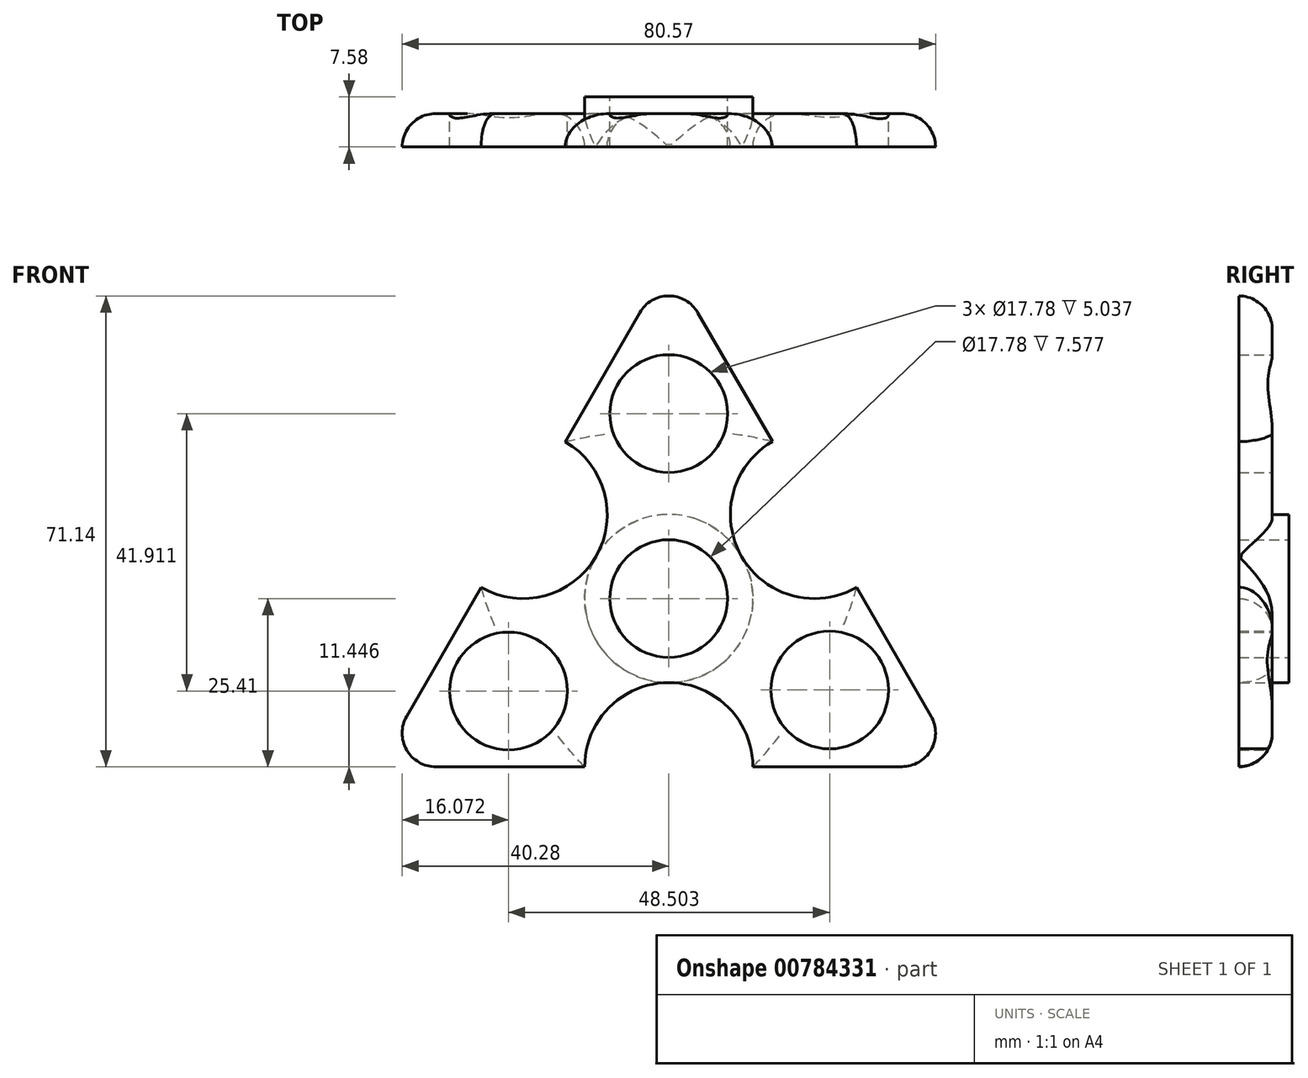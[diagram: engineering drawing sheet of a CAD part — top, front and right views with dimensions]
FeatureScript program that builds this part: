
annotation { "Feature Type Name" : "Feature", "Feature Type Description" : "" }
export const myFeature = defineFeature(function(context is Context, id is Id, definition is map)
    precondition{}
    {
        {
            var Q0;
            Q0=qCreatedBy(makeId("Front.planeOp"),FACE);
            var sketch = newSketch(context, id + "F0", { "sketchPlane" : qUnion([Q0])});
            skCircle(sketch, "E0.cCircle", {"center": v(0, 0) * mm, "radius": 25.4 * mm, "construction": true});
            skLineSegment(sketch, "E0.0", {"start": v(-0.01, 50.8) * mm, "end": v(44, -25.4) * mm});
            skLineSegment(sketch, "E0.1", {"start": v(44, -25.4) * mm, "end": v(-44, -25.41) * mm});
            skLineSegment(sketch, "E0.2", {"start": v(-44, -25.41) * mm, "end": v(-0.01, 50.8) * mm});
            skPoint(sketch, "E0.0.midPoint", {"position": v(22, 12.7) * mm});
            skCircle(sketch, "E1", {"center": v(-22, 12.7) * mm, "radius": 12.7 * mm});
            skCircle(sketch, "E2", {"center": v(0, -25.4) * mm, "radius": 12.7 * mm});
            skPoint(sketch, "E2.centerSnap0", {"position": v(0, -25.4) * mm});
            skCircle(sketch, "E3", {"center": v(22, 12.7) * mm, "radius": 12.7 * mm});
            skSolve(sketch);
        }
        {
            var Q0;
            {var subQ1=sQuery(id+"F0.wireOp",EDGE,"E0.0");var subQ8=sQuery(id+"F0.wireOp",EDGE,"E0.2");var subQ11=makeQuery(id+"F0.imprint","INTERSECT",VERTEX,{"derivedFrom":[subQ1,subQ8]});Q0=makeQuery(id+"F0.imprint","IMPRINT",FACE,{"disambiguationData":[TD([[makeQuery(id+"F0.imprint","IMPRINT",EDGE,{"disambiguationData":[TD([[subQ11,-1.0]])],"derivedFrom":subQ1}),-1.0]])]});}
            extrude(context, id + "F1", {"entities" : qUnion([Q0]), "depth" : 7.62 * mm, "offsetDistance" : 25.4 * mm});
        }
        {
            var Q0;
            Q0=makeQuery(id+"F1.opExtrude","CAP_FACE",FACE,{"disambiguationData":[OSD([sQuery(id+"F0.wireOp",EDGE,"E0.0"),sQuery(id+"F0.wireOp",EDGE,"E0.1"),sQuery(id+"F0.wireOp",EDGE,"E0.2"),sQuery(id+"F0.wireOp",EDGE,"E1"),sQuery(id+"F0.wireOp",EDGE,"E2"),sQuery(id+"F0.wireOp",EDGE,"E3")])],"isStart":false});
            var sketch = newSketch(context, id + "F2", { "sketchPlane" : qUnion([Q0])});
            skCircle(sketch, "E4", {"center": v(0, 0) * mm, "radius": 12.7 * mm});
            skSolve(sketch);
        }
        {
            var Q0;
            Q0=qSketchRegion(id+"F2",true);
            extrude(context, id + "F3", {"entities" : qUnion([Q0]), "operationType" : NewBodyOperationType.ADD, "depth" : 2.54 * mm, "offsetDistance" : 25.4 * mm, "hasSecondDirection" : true, "secondDirectionOppositeDirection" : true, "secondDirectionDepth" : 10.16 * mm});
        }
        {
            var Q0;
            Q0=makeQuery(id+"F3.opExtrude","CAP_FACE",FACE,{"disambiguationData":[OSD([sQuery(id+"F2.wireOp",EDGE,"E4")])],"isStart":true});
            var sketch = newSketch(context, id + "F4", { "sketchPlane" : qUnion([Q0])});
            skCircle(sketch, "E5", {"center": v(0, 0) * mm, "radius": 8.9 * mm});
            skSolve(sketch);
        }
        {
            var Q0;
            Q0=qSketchRegion(id+"F4",true);
            extrude(context, id + "F5", {"entities" : qUnion([Q0]), "operationType" : NewBodyOperationType.REMOVE, "oppositeDirection" : true, "depth" : 25.4 * mm, "offsetDistance" : 25.4 * mm});
        }
        {
            var Q0;
            Q0=qCreatedBy(makeId("Top.planeOp"),FACE);
            var sketch = newSketch(context, id + "F6", { "sketchPlane" : qUnion([Q0])});
            skLineSegment(sketch, "E6.bottom", {"start": v(-45.33, -5.04) * mm, "end": v(58.86, -5.04) * mm});
            skLineSegment(sketch, "E6.top", {"start": v(-45.33, -12.1) * mm, "end": v(58.86, -12.1) * mm});
            skLineSegment(sketch, "E6.left", {"start": v(-45.33, -5.04) * mm, "end": v(-45.33, -12.1) * mm});
            skLineSegment(sketch, "E6.right", {"start": v(58.86, -5.04) * mm, "end": v(58.86, -12.1) * mm});
            skSolve(sketch);
        }
        {
            var Q0;
            Q0=qSketchRegion(id+"F6",true);
            extrude(context, id + "F7", {"entities" : qUnion([Q0]), "operationType" : NewBodyOperationType.REMOVE, "depth" : 66.04 * mm, "offsetDistance" : 25.4 * mm, "hasSecondDirection" : true, "secondDirectionOppositeDirection" : true, "secondDirectionDepth" : 38.86 * mm});
        }
        {
            var Q0;
            Q0=makeQuery(id+"F1.opExtrude","CAP_FACE",FACE,{"disambiguationData":[OSD([sQuery(id+"F0.wireOp",EDGE,"E0.0"),sQuery(id+"F0.wireOp",EDGE,"E0.1"),sQuery(id+"F0.wireOp",EDGE,"E0.2"),sQuery(id+"F0.wireOp",EDGE,"E1"),sQuery(id+"F0.wireOp",EDGE,"E2"),sQuery(id+"F0.wireOp",EDGE,"E3")])],"isStart":true});
            var sketch = newSketch(context, id + "F8", { "sketchPlane" : qUnion([Q0])});
            skCircle(sketch, "E7", {"center": v(0, 27.95) * mm, "radius": 8.9 * mm});
            skCircle(sketch, "E8", {"center": v(-24.3, -13.82) * mm, "radius": 8.9 * mm});
            skCircle(sketch, "E9", {"center": v(24.2, -13.96) * mm, "radius": 8.9 * mm});
            skSolve(sketch);
        }
        {
            var Q0;
            Q0=qSketchRegion(id+"F8",true);
            extrude(context, id + "F9", {"entities" : qUnion([Q0]), "operationType" : NewBodyOperationType.REMOVE, "oppositeDirection" : true, "depth" : 25.4 * mm, "offsetDistance" : 25.4 * mm});
        }
        {
            var Q0;
            Q0=makeQuery(id+"F1.opExtrude","SWEPT_EDGE",EDGE,{"disambiguationData":[OSD([sQuery(id+"F0.wireOp",EDGE,"E0.0"),sQuery(id+"F0.wireOp",EDGE,"E0.2")])]});
            var Q1;
            Q1=makeQuery(id+"F1.opExtrude","SWEPT_EDGE",EDGE,{"disambiguationData":[OSD([sQuery(id+"F0.wireOp",EDGE,"E0.0"),sQuery(id+"F0.wireOp",EDGE,"E0.1")])]});
            var Q2;
            Q2=makeQuery(id+"F1.opExtrude","SWEPT_EDGE",EDGE,{"disambiguationData":[OSD([sQuery(id+"F0.wireOp",EDGE,"E0.1"),sQuery(id+"F0.wireOp",EDGE,"E0.2")])]});
            fillet(context, id + "F10", {"entities" : qUnion([Q0, Q1, Q2]), "radius" : 5.08 * mm, "tangentPropagation" : true, "allowEdgeOverflow" : false});
        }
        {
            var Q0;
            {var subQ0=sQuery(id+"F0.wireOp",EDGE,"E0.1");Q0=makeQuery(id+"F1.opExtrude","CAP_EDGE",EDGE,{"disambiguationData":[OSD([subQ0]),TDD([makeQuery(id+"F0.imprint","IMPRINT",EDGE,{"disambiguationData":[TD([[makeQuery(id+"F0.imprint","INTERSECT",VERTEX,{"derivedFrom":[subQ0,sQuery(id+"F0.wireOp",EDGE,"E0.2")]}),1.0]])],"derivedFrom":subQ0})])],"isStart":true});}
            var Q1;
            {var subQ0=sQuery(id+"F0.wireOp",EDGE,"E0.1");Q1=makeQuery(id+"F1.opExtrude","CAP_EDGE",EDGE,{"disambiguationData":[OSD([subQ0]),TDD([makeQuery(id+"F0.imprint","IMPRINT",EDGE,{"disambiguationData":[TD([[makeQuery(id+"F0.imprint","INTERSECT",VERTEX,{"derivedFrom":[sQuery(id+"F0.wireOp",EDGE,"E0.0"),subQ0]}),-1.0]])],"derivedFrom":subQ0})])],"isStart":true});}
            var Q2;
            {var subQ0=sQuery(id+"F0.wireOp",EDGE,"E0.0");Q2=makeQuery(id+"F1.opExtrude","CAP_EDGE",EDGE,{"disambiguationData":[OSD([subQ0]),TDD([makeQuery(id+"F0.imprint","IMPRINT",EDGE,{"disambiguationData":[TD([[makeQuery(id+"F0.imprint","INTERSECT",VERTEX,{"derivedFrom":[subQ0,sQuery(id+"F0.wireOp",EDGE,"E0.2")]}),-1.0]])],"derivedFrom":subQ0})])],"isStart":true});}
            var Q3;
            Q3=makeQuery(id+"F1.opExtrude","CAP_EDGE",EDGE,{"disambiguationData":[OSD([sQuery(id+"F0.wireOp",EDGE,"E3")])],"isStart":true});
            var Q4;
            Q4=makeQuery(id+"F1.opExtrude","CAP_EDGE",EDGE,{"disambiguationData":[OSD([sQuery(id+"F0.wireOp",EDGE,"E1")])],"isStart":true});
            var Q5;
            Q5=makeQuery(id+"F1.opExtrude","CAP_EDGE",EDGE,{"disambiguationData":[OSD([sQuery(id+"F0.wireOp",EDGE,"E2")])],"isStart":true});
            fillet(context, id + "F11", {"entities" : qUnion([Q0, Q1, Q2, Q3, Q4, Q5]), "radius" : 5.08 * mm, "tangentPropagation" : true, "allowEdgeOverflow" : false});
        }
    });
